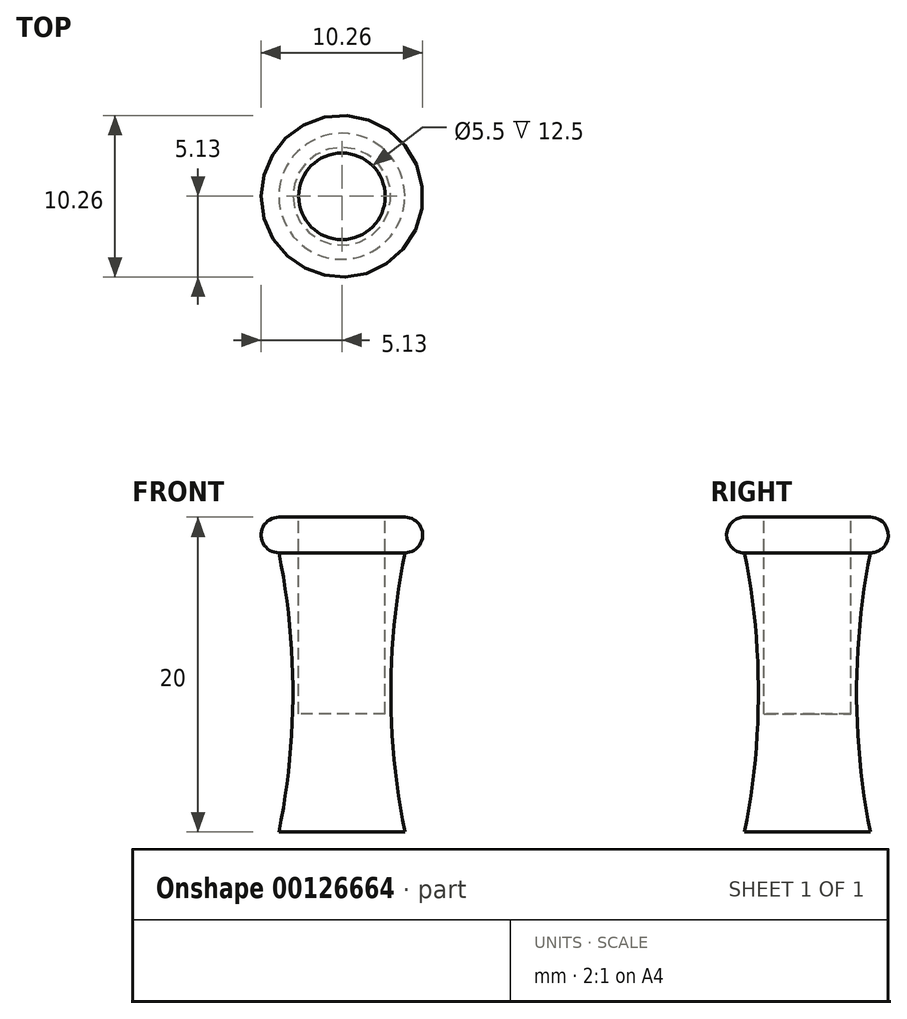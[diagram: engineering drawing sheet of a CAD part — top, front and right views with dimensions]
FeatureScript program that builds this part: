
annotation { "Feature Type Name" : "Feature", "Feature Type Description" : "" }
export const myFeature = defineFeature(function(context is Context, id is Id, definition is map)
    precondition{}
    {
        {
            var Q0;
            Q0=qCreatedBy(makeId("Front.planeOp"),FACE);
            var sketch = newSketch(context, id + "F0", { "sketchPlane" : qUnion([Q0])});
            skLineSegment(sketch, "E0", {"start": v(0, 0) * mm, "end": v(0, 20) * mm});
            skLineSegment(sketch, "E1", {"start": v(0, 20) * mm, "end": v(4, 20) * mm});
            skLineSegment(sketch, "E2", {"start": v(0, 0) * mm, "end": v(4, 0) * mm});
            skArc(sketch, "E3", {"start": v(4, 17.73) * mm, "mid": v(5.13, 18.87) * mm, "end": v(4, 20) * mm});
            skArc(sketch, "E4", {"start": v(4, 17.73) * mm, "mid": v(3.12, 8.87) * mm, "end": v(4, 0) * mm});
            skSolve(sketch);
        }
        {
            var Q0;
            Q0=makeQuery(id+"F0.imprint","IMPRINT",FACE,{"disambiguationData":[TD([[makeQuery(id+"F0.imprint","IMPRINT",EDGE,{"derivedFrom":sQuery(id+"F0.wireOp",EDGE,"E0")}),-1.0]])]});
            var Q1;
            Q1=sQuery(id+"F0.wireOp",EDGE,"E0");
            revolve(context, id + "F1", {"entities" : qUnion([Q0]), "axis" : qUnion([Q1]), "revolveType" : RevolveType.FULL});
        }
        {
            var Q0;
            Q0=makeQuery(id+"F1.opRevolve","SWEPT_FACE",FACE,{"disambiguationData":[OSD([sQuery(id+"F0.wireOp",EDGE,"E1")])]});
            var sketch = newSketch(context, id + "F2", { "sketchPlane" : qUnion([Q0])});
            skCircle(sketch, "E5", {"center": v(0, 0) * mm, "radius": 2.75 * mm});
            skSolve(sketch);
        }
        {
            var Q0;
            Q0=makeQuery(id+"F2.imprint","IMPRINT",FACE,{"disambiguationData":[TD([[makeQuery(id+"F2.imprint","IMPRINT",EDGE,{"derivedFrom":sQuery(id+"F2.wireOp",EDGE,"E5")}),1.0]])]});
            extrude(context, id + "F3", {"entities" : qUnion([Q0]), "operationType" : NewBodyOperationType.REMOVE, "oppositeDirection" : true, "depth" : 12.5 * mm});
        }
    });
